# Revit family: 9101
name_source: partatom
category: Doors
revit_build: Autodesk Revit LT 2016 (Build: 20150220_1215(x64)
units: mm (PartAtom-declared; Revit-internal decimal feet)

## family parameters
Always vertical = Yes
Cut with Voids When Loaded = No
Host = Wall
OmniClass Number = 23.30.10.00
OmniClass Title = Doors
Room Calculation Point = No
Shared = No

## types (1)
- 1788x2088mm
    Bottom Placement = 99 mm  [stored 0.324803 ft]
    Frame Projection Ext. = 25 mm  [stored 0.082021 ft]
    Frame Projection Int. = 25 mm  [stored 0.082021 ft]
    Frame Width = 75 mm  [stored 0.246063 ft]
    Function = Interior
    Height = 2088 mm
    Joint = 12 mm  [stored 0.0393701 ft]
    Manufacturer = www.kronevinduer.dk
    Placement in wall = 40 mm  [stored 0.131234 ft]
    Rough Height = 2112 mm  [stored 6.92913 ft]
    Rough Width = 1812 mm  [stored 5.94488 ft]
    Wall Closure = By host
    Width = 1788 mm
    Width left leaf = 894 mm

note: [stored X ft] marks values corroborated as IEEE doubles in the binary element streams (Revit-internal decimal feet)

## geometry (parser evidence)
native form markers: Sweep x6
no freeform markers — native parametric forms only
